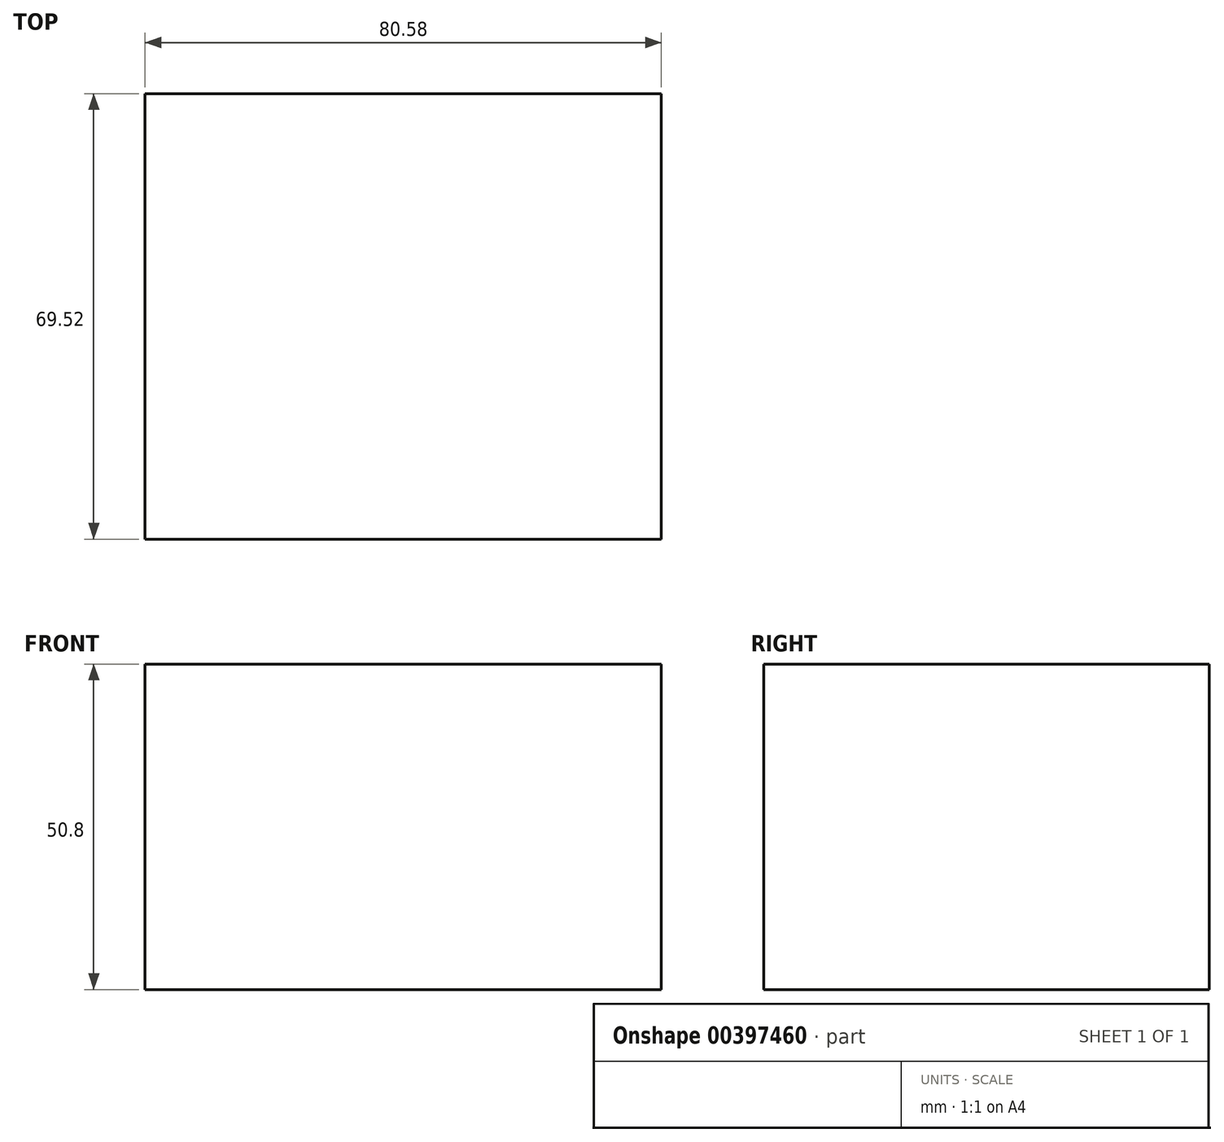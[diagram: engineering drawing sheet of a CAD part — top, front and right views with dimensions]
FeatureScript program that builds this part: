
annotation { "Feature Type Name" : "Feature", "Feature Type Description" : "" }
export const myFeature = defineFeature(function(context is Context, id is Id, definition is map)
    precondition{}
    {
        {
            var Q0;
            Q0=qCreatedBy(makeId("Top.planeOp"),FACE);
            var sketch = newSketch(context, id + "F0", { "sketchPlane" : qUnion([Q0])});
            skLineSegment(sketch, "E0.bottom", {"start": v(-37.13, 38.26) * mm, "end": v(43.45, 38.26) * mm});
            skLineSegment(sketch, "E0.top", {"start": v(-37.13, -31.26) * mm, "end": v(43.45, -31.26) * mm});
            skLineSegment(sketch, "E0.left", {"start": v(-37.13, 38.26) * mm, "end": v(-37.13, -31.26) * mm});
            skLineSegment(sketch, "E0.right", {"start": v(43.45, 38.26) * mm, "end": v(43.45, -31.26) * mm});
            skSolve(sketch);
        }
        {
            var Q0;
            Q0 = qSketchRegion(id + "F0", true);
            extrude(context, id + "F1", {"entities" : qUnion([Q0]), "depth" : 50.8 * mm});
        }
    });
